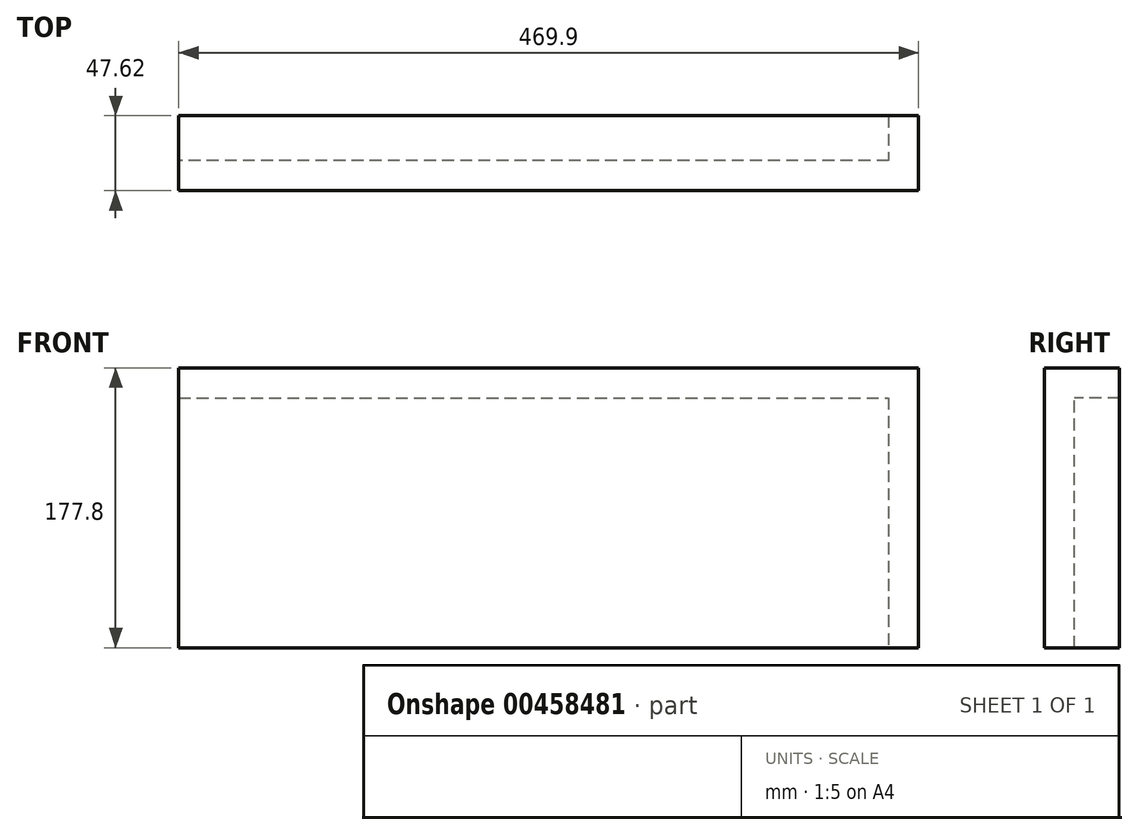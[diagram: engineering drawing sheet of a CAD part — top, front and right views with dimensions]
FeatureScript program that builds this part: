
annotation { "Feature Type Name" : "Feature", "Feature Type Description" : "" }
export const myFeature = defineFeature(function(context is Context, id is Id, definition is map)
    precondition{}
    {
        {
            var Q0;
            Q0=qCreatedBy(makeId("Front.planeOp"),FACE);
            var sketch = newSketch(context, id + "F0", { "sketchPlane" : qUnion([Q0])});
            skLineSegment(sketch, "E0", {"start": v(0, 0) * mm, "end": v(0, 177.8) * mm});
            skLineSegment(sketch, "E1", {"start": v(0, 177.8) * mm, "end": v(469.9, 177.8) * mm});
            skLineSegment(sketch, "E2", {"start": v(469.9, 177.8) * mm, "end": v(469.9, 0) * mm});
            skLineSegment(sketch, "E3", {"start": v(469.9, 0) * mm, "end": v(0, 0) * mm});
            skSolve(sketch);
        }
        {
            var Q0;
            Q0=makeQuery(id+"F0.imprint","IMPRINT",FACE,{"disambiguationData":[TD([[makeQuery(id+"F0.imprint","IMPRINT",EDGE,{"derivedFrom":sQuery(id+"F0.wireOp",EDGE,"E0")}),-1.0]])]});
            extrude(context, id + "F1", {"entities" : qUnion([Q0]), "oppositeDirection" : true, "depth" : 19.05 * mm});
        }
        {
            var Q0;
            Q0=makeQuery(id+"F1.opExtrude","CAP_FACE",FACE,{"disambiguationData":[OSD([sQuery(id+"F0.wireOp",EDGE,"E0"),sQuery(id+"F0.wireOp",EDGE,"E1"),sQuery(id+"F0.wireOp",EDGE,"E2"),sQuery(id+"F0.wireOp",EDGE,"E3")])],"isStart":false});
            var sketch = newSketch(context, id + "F2", { "sketchPlane" : qUnion([Q0])});
            skLineSegment(sketch, "E4", {"start": v(-469.9, 0) * mm, "end": v(-469.9, 177.8) * mm});
            skLineSegment(sketch, "E5", {"start": v(-469.9, 177.8) * mm, "end": v(0, 177.8) * mm});
            skLineSegment(sketch, "E6", {"start": v(0, 177.8) * mm, "end": v(0, 158.75) * mm});
            skLineSegment(sketch, "E7", {"start": v(0, 158.75) * mm, "end": v(-450.85, 158.75) * mm});
            skLineSegment(sketch, "E8", {"start": v(-450.85, 158.75) * mm, "end": v(-450.85, 0) * mm});
            skLineSegment(sketch, "E9", {"start": v(-450.85, 0) * mm, "end": v(-469.9, 0) * mm});
            skSolve(sketch);
        }
        {
            var Q0;
            Q0=makeQuery(id+"F2.imprint","IMPRINT",FACE,{"disambiguationData":[TD([[makeQuery(id+"F2.imprint","IMPRINT",EDGE,{"derivedFrom":sQuery(id+"F2.wireOp",EDGE,"E4")}),1.0]])]});
            extrude(context, id + "F3", {"entities" : qUnion([Q0]), "operationType" : NewBodyOperationType.ADD, "depth" : 28.57 * mm});
        }
    });
